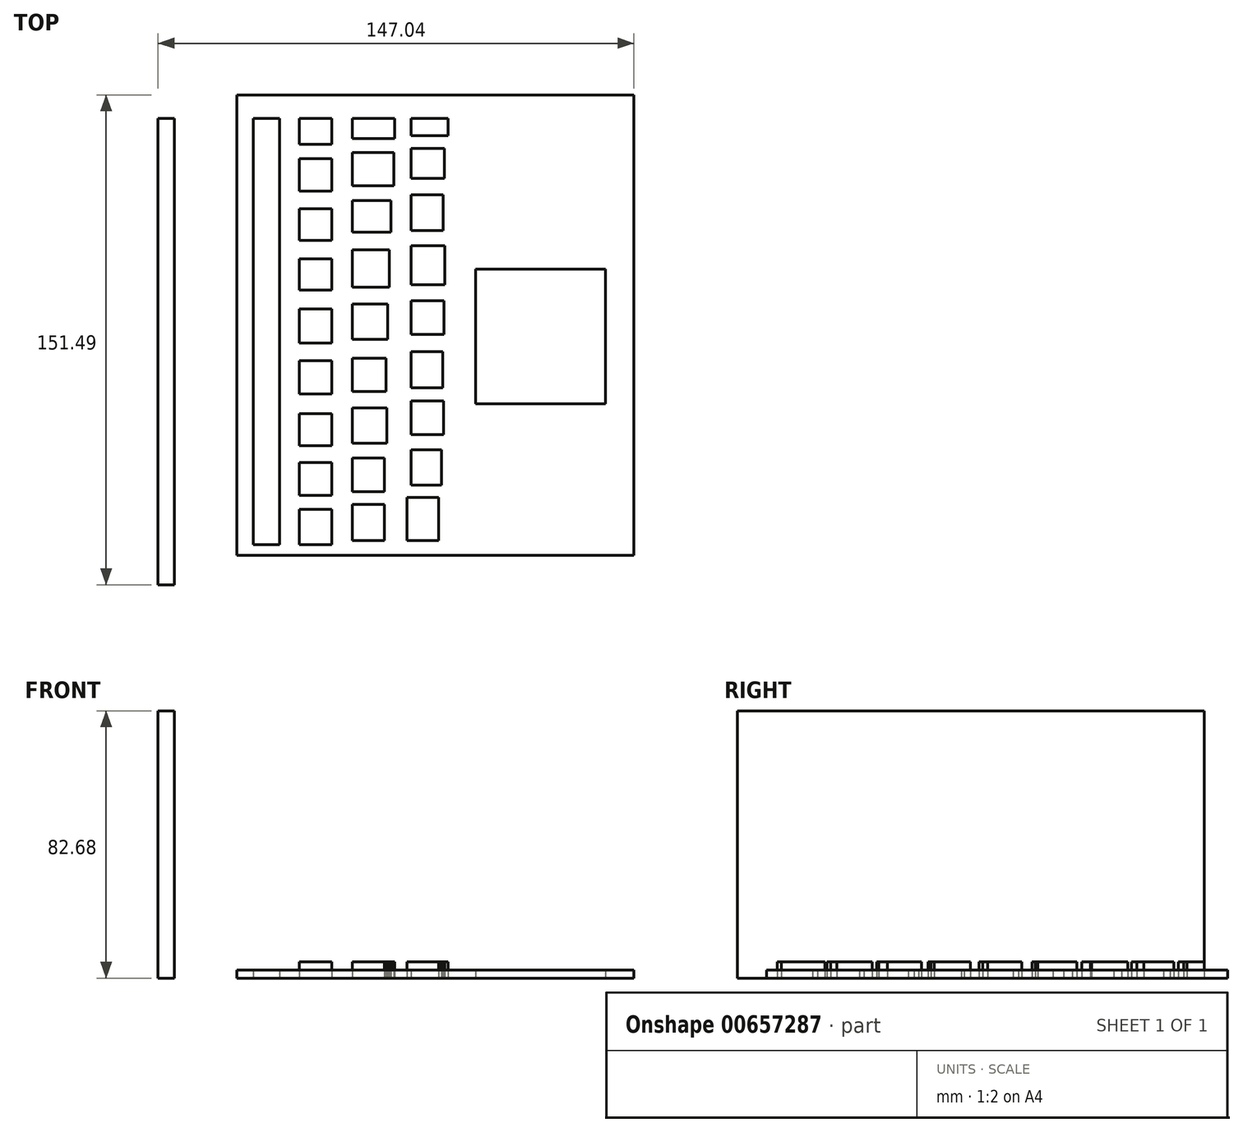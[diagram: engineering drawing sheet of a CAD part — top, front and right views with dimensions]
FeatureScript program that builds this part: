
annotation { "Feature Type Name" : "Feature", "Feature Type Description" : "" }
export const myFeature = defineFeature(function(context is Context, id is Id, definition is map)
    precondition{}
    {
        {
            var Q0;
            Q0=qCreatedBy(makeId("Right.planeOp"),FACE);
            var sketch = newSketch(context, id + "F0", { "sketchPlane" : qUnion([Q0])});
            skLineSegment(sketch, "E0.bottom", {"start": v(-144.27, 82.68) * mm, "end": v(0, 82.68) * mm});
            skLineSegment(sketch, "E0.top", {"start": v(-144.27, 0) * mm, "end": v(0, 0) * mm});
            skLineSegment(sketch, "E0.left", {"start": v(-144.27, 82.68) * mm, "end": v(-144.27, 0) * mm});
            skLineSegment(sketch, "E0.right", {"start": v(0, 82.68) * mm, "end": v(0, 0) * mm});
            skSolve(sketch);
        }
        {
            var Q0;
            Q0=qCreatedBy(makeId("Top.planeOp"),FACE);
            var sketch = newSketch(context, id + "F1", { "sketchPlane" : qUnion([Q0])});
            skLineSegment(sketch, "E1.bottom", {"start": v(24.3, -135.23) * mm, "end": v(147.04, -135.23) * mm});
            skLineSegment(sketch, "E1.top", {"start": v(24.3, 7.22) * mm, "end": v(147.04, 7.22) * mm});
            skLineSegment(sketch, "E1.left", {"start": v(24.3, -135.23) * mm, "end": v(24.3, 7.22) * mm});
            skLineSegment(sketch, "E1.right", {"start": v(147.04, -135.23) * mm, "end": v(147.04, 7.22) * mm});
            skLineSegment(sketch, "E2.bottom", {"start": v(98.13, -88.3) * mm, "end": v(138.28, -88.3) * mm});
            skLineSegment(sketch, "E2.top", {"start": v(98.13, -46.73) * mm, "end": v(138.28, -46.73) * mm});
            skLineSegment(sketch, "E2.left", {"start": v(98.13, -88.3) * mm, "end": v(98.13, -46.73) * mm});
            skLineSegment(sketch, "E2.right", {"start": v(138.28, -88.3) * mm, "end": v(138.28, -46.73) * mm});
            skLineSegment(sketch, "E3.bottom", {"start": v(29.4, -131.89) * mm, "end": v(37.55, -131.89) * mm});
            skLineSegment(sketch, "E3.top", {"start": v(29.4, 0) * mm, "end": v(37.55, 0) * mm});
            skLineSegment(sketch, "E3.left", {"start": v(29.4, -131.89) * mm, "end": v(29.4, 0) * mm});
            skLineSegment(sketch, "E3.right", {"start": v(37.55, -131.89) * mm, "end": v(37.55, 0) * mm});
            skLineSegment(sketch, "E4.bottom", {"start": v(43.69, -131.89) * mm, "end": v(53.65, -131.89) * mm});
            skLineSegment(sketch, "E4.top", {"start": v(43.69, -121.02) * mm, "end": v(53.65, -121.02) * mm});
            skLineSegment(sketch, "E4.left", {"start": v(43.69, -131.89) * mm, "end": v(43.69, -121.02) * mm});
            skLineSegment(sketch, "E4.right", {"start": v(53.65, -131.89) * mm, "end": v(53.65, -121.02) * mm});
            skLineSegment(sketch, "E5.bottom", {"start": v(43.69, -116.6) * mm, "end": v(53.65, -116.6) * mm});
            skLineSegment(sketch, "E5.top", {"start": v(43.69, -106.49) * mm, "end": v(53.65, -106.49) * mm});
            skLineSegment(sketch, "E5.left", {"start": v(43.69, -116.6) * mm, "end": v(43.69, -106.49) * mm});
            skLineSegment(sketch, "E5.right", {"start": v(53.65, -116.6) * mm, "end": v(53.65, -106.49) * mm});
            skLineSegment(sketch, "E6.bottom", {"start": v(43.69, -101.23) * mm, "end": v(53.65, -101.23) * mm});
            skLineSegment(sketch, "E6.top", {"start": v(43.69, -91.38) * mm, "end": v(53.65, -91.38) * mm});
            skLineSegment(sketch, "E6.left", {"start": v(43.69, -101.23) * mm, "end": v(43.69, -91.38) * mm});
            skLineSegment(sketch, "E6.right", {"start": v(53.65, -101.23) * mm, "end": v(53.65, -91.38) * mm});
            skLineSegment(sketch, "E7.bottom", {"start": v(43.69, -85.34) * mm, "end": v(53.65, -85.34) * mm});
            skLineSegment(sketch, "E7.top", {"start": v(43.69, -75.04) * mm, "end": v(53.65, -75.04) * mm});
            skLineSegment(sketch, "E7.left", {"start": v(43.69, -85.34) * mm, "end": v(43.69, -75.04) * mm});
            skLineSegment(sketch, "E7.right", {"start": v(53.65, -85.34) * mm, "end": v(53.65, -75.04) * mm});
            skLineSegment(sketch, "E8.bottom", {"start": v(43.69, -69.58) * mm, "end": v(53.65, -69.58) * mm});
            skLineSegment(sketch, "E8.top", {"start": v(43.69, -59) * mm, "end": v(53.65, -59) * mm});
            skLineSegment(sketch, "E8.left", {"start": v(43.69, -69.58) * mm, "end": v(43.69, -59) * mm});
            skLineSegment(sketch, "E8.right", {"start": v(53.65, -69.58) * mm, "end": v(53.65, -59) * mm});
            skLineSegment(sketch, "E9.bottom", {"start": v(43.69, -53.2) * mm, "end": v(53.65, -53.2) * mm});
            skLineSegment(sketch, "E9.top", {"start": v(43.69, -43.48) * mm, "end": v(53.65, -43.48) * mm});
            skLineSegment(sketch, "E9.left", {"start": v(43.69, -53.2) * mm, "end": v(43.69, -43.48) * mm});
            skLineSegment(sketch, "E9.right", {"start": v(53.65, -53.2) * mm, "end": v(53.65, -43.48) * mm});
            skLineSegment(sketch, "E10.bottom", {"start": v(43.69, -37.82) * mm, "end": v(53.65, -37.82) * mm});
            skLineSegment(sketch, "E10.top", {"start": v(43.69, -27.98) * mm, "end": v(53.65, -27.98) * mm});
            skLineSegment(sketch, "E10.left", {"start": v(43.69, -37.82) * mm, "end": v(43.69, -27.98) * mm});
            skLineSegment(sketch, "E10.right", {"start": v(53.65, -37.82) * mm, "end": v(53.65, -27.98) * mm});
            skLineSegment(sketch, "E11.bottom", {"start": v(43.69, -22.52) * mm, "end": v(53.65, -22.52) * mm});
            skLineSegment(sketch, "E11.top", {"start": v(43.69, -12.52) * mm, "end": v(53.65, -12.52) * mm});
            skLineSegment(sketch, "E11.left", {"start": v(43.69, -22.52) * mm, "end": v(43.69, -12.52) * mm});
            skLineSegment(sketch, "E11.right", {"start": v(53.65, -22.52) * mm, "end": v(53.65, -12.52) * mm});
            skLineSegment(sketch, "E12.bottom", {"start": v(43.69, -8.03) * mm, "end": v(53.65, -8.03) * mm});
            skLineSegment(sketch, "E12.top", {"start": v(43.69, 0) * mm, "end": v(53.65, 0) * mm});
            skLineSegment(sketch, "E12.left", {"start": v(43.69, -8.03) * mm, "end": v(43.69, 0) * mm});
            skLineSegment(sketch, "E12.right", {"start": v(53.65, -8.03) * mm, "end": v(53.65, 0) * mm});
            skLineSegment(sketch, "E13.bottom", {"start": v(60, -130.66) * mm, "end": v(69.95, -130.66) * mm});
            skLineSegment(sketch, "E13.top", {"start": v(60, -119.44) * mm, "end": v(69.95, -119.44) * mm});
            skLineSegment(sketch, "E13.left", {"start": v(60, -130.66) * mm, "end": v(60, -119.44) * mm});
            skLineSegment(sketch, "E13.right", {"start": v(69.95, -130.66) * mm, "end": v(69.95, -119.44) * mm});
            skPoint(sketch, "E14.firstSnap0", {"position": v(60, -125.05) * mm});
            skPoint(sketch, "E14.oppositeSnap0", {"position": v(69.95, -125.05) * mm});
            skLineSegment(sketch, "E14.bottom", {"start": v(60, -115.5) * mm, "end": v(69.95, -115.5) * mm});
            skLineSegment(sketch, "E14.top", {"start": v(60, -105.1) * mm, "end": v(69.95, -105.1) * mm});
            skLineSegment(sketch, "E14.left", {"start": v(60, -115.5) * mm, "end": v(60, -105.1) * mm});
            skLineSegment(sketch, "E14.right", {"start": v(69.95, -115.5) * mm, "end": v(69.95, -105.1) * mm});
            skLineSegment(sketch, "E15.bottom", {"start": v(60, -100.52) * mm, "end": v(70.74, -100.52) * mm});
            skLineSegment(sketch, "E15.top", {"start": v(60, -89.64) * mm, "end": v(70.74, -89.64) * mm});
            skLineSegment(sketch, "E15.left", {"start": v(60, -100.52) * mm, "end": v(60, -89.64) * mm});
            skLineSegment(sketch, "E15.right", {"start": v(70.74, -100.52) * mm, "end": v(70.74, -89.64) * mm});
            skLineSegment(sketch, "E16.bottom", {"start": v(60, -84.48) * mm, "end": v(70.42, -84.48) * mm});
            skLineSegment(sketch, "E16.top", {"start": v(60, -74.18) * mm, "end": v(70.42, -74.18) * mm});
            skLineSegment(sketch, "E16.left", {"start": v(60, -84.48) * mm, "end": v(60, -74.18) * mm});
            skLineSegment(sketch, "E16.right", {"start": v(70.42, -84.48) * mm, "end": v(70.42, -74.18) * mm});
            skLineSegment(sketch, "E17.bottom", {"start": v(60, -68.38) * mm, "end": v(70.93, -68.38) * mm});
            skLineSegment(sketch, "E17.top", {"start": v(60, -57.45) * mm, "end": v(70.93, -57.45) * mm});
            skLineSegment(sketch, "E17.left", {"start": v(60, -68.38) * mm, "end": v(60, -57.45) * mm});
            skLineSegment(sketch, "E17.right", {"start": v(70.93, -68.38) * mm, "end": v(70.93, -57.45) * mm});
            skLineSegment(sketch, "E18.bottom", {"start": v(60, -52.24) * mm, "end": v(71.44, -52.24) * mm});
            skLineSegment(sketch, "E18.top", {"start": v(60, -40.73) * mm, "end": v(71.44, -40.73) * mm});
            skLineSegment(sketch, "E18.left", {"start": v(60, -52.24) * mm, "end": v(60, -40.73) * mm});
            skLineSegment(sketch, "E18.right", {"start": v(71.44, -52.24) * mm, "end": v(71.44, -40.73) * mm});
            skLineSegment(sketch, "E19.bottom", {"start": v(60, -35.22) * mm, "end": v(72.05, -35.22) * mm});
            skLineSegment(sketch, "E19.top", {"start": v(60, -25.51) * mm, "end": v(72.05, -25.51) * mm});
            skLineSegment(sketch, "E19.left", {"start": v(60, -35.22) * mm, "end": v(60, -25.51) * mm});
            skLineSegment(sketch, "E19.right", {"start": v(72.05, -35.22) * mm, "end": v(72.05, -25.51) * mm});
            skLineSegment(sketch, "E20.bottom", {"start": v(60, -20.84) * mm, "end": v(72.82, -20.84) * mm});
            skLineSegment(sketch, "E20.top", {"start": v(60, -10.6) * mm, "end": v(72.82, -10.6) * mm});
            skLineSegment(sketch, "E20.left", {"start": v(60, -20.84) * mm, "end": v(60, -10.6) * mm});
            skLineSegment(sketch, "E20.right", {"start": v(72.82, -20.84) * mm, "end": v(72.82, -10.6) * mm});
            skLineSegment(sketch, "E21.bottom", {"start": v(60, -6.3) * mm, "end": v(73.1, -6.3) * mm});
            skLineSegment(sketch, "E21.top", {"start": v(60, 0) * mm, "end": v(73.1, 0) * mm});
            skLineSegment(sketch, "E21.left", {"start": v(60, -6.3) * mm, "end": v(60, 0) * mm});
            skLineSegment(sketch, "E21.right", {"start": v(73.1, -6.3) * mm, "end": v(73.1, 0) * mm});
            skLineSegment(sketch, "E22.bottom", {"start": v(76.97, -130.66) * mm, "end": v(86.66, -130.66) * mm});
            skLineSegment(sketch, "E22.top", {"start": v(76.97, -117.22) * mm, "end": v(86.66, -117.22) * mm});
            skLineSegment(sketch, "E22.left", {"start": v(76.97, -130.66) * mm, "end": v(76.97, -117.22) * mm});
            skLineSegment(sketch, "E22.right", {"start": v(86.66, -130.66) * mm, "end": v(86.66, -117.22) * mm});
            skLineSegment(sketch, "E23.bottom", {"start": v(78.24, -113.48) * mm, "end": v(87.6, -113.48) * mm});
            skLineSegment(sketch, "E23.top", {"start": v(78.24, -102.6) * mm, "end": v(87.6, -102.6) * mm});
            skLineSegment(sketch, "E23.left", {"start": v(78.24, -113.48) * mm, "end": v(78.24, -102.6) * mm});
            skLineSegment(sketch, "E23.right", {"start": v(87.6, -113.48) * mm, "end": v(87.6, -102.6) * mm});
            skLineSegment(sketch, "E24.bottom", {"start": v(78.24, -97.88) * mm, "end": v(88.2, -97.88) * mm});
            skLineSegment(sketch, "E24.top", {"start": v(78.24, -87.38) * mm, "end": v(88.2, -87.38) * mm});
            skLineSegment(sketch, "E24.left", {"start": v(78.24, -97.88) * mm, "end": v(78.24, -87.38) * mm});
            skLineSegment(sketch, "E24.right", {"start": v(88.2, -97.88) * mm, "end": v(88.2, -87.38) * mm});
            skLineSegment(sketch, "E25.bottom", {"start": v(78.24, -83.39) * mm, "end": v(88.06, -83.39) * mm});
            skLineSegment(sketch, "E25.top", {"start": v(78.24, -72.2) * mm, "end": v(88.06, -72.2) * mm});
            skLineSegment(sketch, "E25.left", {"start": v(78.24, -83.39) * mm, "end": v(78.24, -72.2) * mm});
            skLineSegment(sketch, "E25.right", {"start": v(88.06, -83.39) * mm, "end": v(88.06, -72.2) * mm});
            skLineSegment(sketch, "E26.bottom", {"start": v(78.24, -66.9) * mm, "end": v(88.32, -66.9) * mm});
            skLineSegment(sketch, "E26.top", {"start": v(78.24, -56.4) * mm, "end": v(88.32, -56.4) * mm});
            skLineSegment(sketch, "E26.left", {"start": v(78.24, -66.9) * mm, "end": v(78.24, -56.4) * mm});
            skLineSegment(sketch, "E26.right", {"start": v(88.32, -66.9) * mm, "end": v(88.32, -56.4) * mm});
            skLineSegment(sketch, "E27.bottom", {"start": v(78.24, -51.45) * mm, "end": v(88.67, -51.45) * mm});
            skLineSegment(sketch, "E27.top", {"start": v(78.24, -39.39) * mm, "end": v(88.67, -39.39) * mm});
            skLineSegment(sketch, "E27.left", {"start": v(78.24, -51.45) * mm, "end": v(78.24, -39.39) * mm});
            skLineSegment(sketch, "E27.right", {"start": v(88.67, -51.45) * mm, "end": v(88.67, -39.39) * mm});
            skLineSegment(sketch, "E28.bottom", {"start": v(78.24, -34.76) * mm, "end": v(88.18, -34.76) * mm});
            skLineSegment(sketch, "E28.top", {"start": v(78.24, -23.63) * mm, "end": v(88.18, -23.63) * mm});
            skLineSegment(sketch, "E28.left", {"start": v(78.24, -34.76) * mm, "end": v(78.24, -23.63) * mm});
            skLineSegment(sketch, "E28.right", {"start": v(88.18, -34.76) * mm, "end": v(88.18, -23.63) * mm});
            skLineSegment(sketch, "E29.bottom", {"start": v(78.24, -18.62) * mm, "end": v(88.53, -18.62) * mm});
            skLineSegment(sketch, "E29.top", {"start": v(78.24, -9.34) * mm, "end": v(88.53, -9.34) * mm});
            skLineSegment(sketch, "E29.left", {"start": v(78.24, -18.62) * mm, "end": v(78.24, -9.34) * mm});
            skLineSegment(sketch, "E29.right", {"start": v(88.53, -18.62) * mm, "end": v(88.53, -9.34) * mm});
            skLineSegment(sketch, "E30.bottom", {"start": v(78.24, -5.35) * mm, "end": v(89.58, -5.35) * mm});
            skLineSegment(sketch, "E30.top", {"start": v(78.24, 0) * mm, "end": v(89.58, 0) * mm});
            skLineSegment(sketch, "E30.left", {"start": v(78.24, -5.35) * mm, "end": v(78.24, 0) * mm});
            skLineSegment(sketch, "E30.right", {"start": v(89.58, -5.35) * mm, "end": v(89.58, 0) * mm});
            skSolve(sketch);
        }
        {
            var Q0;
            Q0=makeQuery(id+"F0.imprint","IMPRINT",FACE,{"disambiguationData":[TD([[makeQuery(id+"F0.imprint","IMPRINT",EDGE,{"derivedFrom":sQuery(id+"F0.wireOp",EDGE,"E0.bottom")}),-1.0]])]});
            extrude(context, id + "F2", {"entities" : qUnion([Q0]), "depth" : 5.08 * mm, "offsetDistance" : 25.4 * mm});
        }
        {
            var Q0;
            Q0=makeQuery(id+"F1.imprint","IMPRINT",FACE,{"disambiguationData":[TD([[makeQuery(id+"F1.imprint","IMPRINT",EDGE,{"derivedFrom":sQuery(id+"F1.wireOp",EDGE,"E2.bottom")}),1.0]])]});
            extrude(context, id + "F3", {"entities" : qUnion([Q0]), "depth" : 2.54 * mm, "offsetDistance" : 25.4 * mm});
        }
        {
            var Q0;
            Q0=makeQuery(id+"F1.imprint","IMPRINT",FACE,{"disambiguationData":[TD([[makeQuery(id+"F1.imprint","IMPRINT",EDGE,{"derivedFrom":sQuery(id+"F1.wireOp",EDGE,"E3.bottom")}),1.0]])]});
            extrude(context, id + "F4", {"entities" : qUnion([Q0]), "depth" : 2.54 * mm, "offsetDistance" : 25.4 * mm});
        }
        {
            var Q0;
            Q0=makeQuery(id+"F1.imprint","IMPRINT",FACE,{"disambiguationData":[TD([[makeQuery(id+"F1.imprint","IMPRINT",EDGE,{"derivedFrom":sQuery(id+"F1.wireOp",EDGE,"E11.bottom")}),1.0]])]});
            extrude(context, id + "F5", {"entities" : qUnion([Q0]), "depth" : 5.08 * mm, "offsetDistance" : 25.4 * mm});
        }
        {
            var Q0;
            Q0=makeQuery(id+"F1.imprint","IMPRINT",FACE,{"disambiguationData":[TD([[makeQuery(id+"F1.imprint","IMPRINT",EDGE,{"derivedFrom":sQuery(id+"F1.wireOp",EDGE,"E10.bottom")}),1.0]])]});
            extrude(context, id + "F6", {"entities" : qUnion([Q0]), "depth" : 5.08 * mm, "offsetDistance" : 25.4 * mm});
        }
        {
            var Q0;
            Q0=makeQuery(id+"F1.imprint","IMPRINT",FACE,{"disambiguationData":[TD([[makeQuery(id+"F1.imprint","IMPRINT",EDGE,{"derivedFrom":sQuery(id+"F1.wireOp",EDGE,"E8.bottom")}),1.0]])]});
            extrude(context, id + "F7", {"entities" : qUnion([Q0]), "depth" : 5.08 * mm, "offsetDistance" : 25.4 * mm});
        }
        {
            var Q0;
            Q0=makeQuery(id+"F1.imprint","IMPRINT",FACE,{"disambiguationData":[TD([[makeQuery(id+"F1.imprint","IMPRINT",EDGE,{"derivedFrom":sQuery(id+"F1.wireOp",EDGE,"E7.bottom")}),1.0]])]});
            extrude(context, id + "F8", {"entities" : qUnion([Q0]), "depth" : 5.08 * mm, "offsetDistance" : 25.4 * mm});
        }
        {
            var Q0;
            Q0=makeQuery(id+"F1.imprint","IMPRINT",FACE,{"disambiguationData":[TD([[makeQuery(id+"F1.imprint","IMPRINT",EDGE,{"derivedFrom":sQuery(id+"F1.wireOp",EDGE,"E9.bottom")}),1.0]])]});
            extrude(context, id + "F9", {"entities" : qUnion([Q0]), "depth" : 5.08 * mm, "offsetDistance" : 25.4 * mm});
        }
        {
            var Q0;
            Q0=makeQuery(id+"F1.imprint","IMPRINT",FACE,{"disambiguationData":[TD([[makeQuery(id+"F1.imprint","IMPRINT",EDGE,{"derivedFrom":sQuery(id+"F1.wireOp",EDGE,"E6.bottom")}),1.0]])]});
            extrude(context, id + "F10", {"entities" : qUnion([Q0]), "depth" : 5.08 * mm, "offsetDistance" : 25.4 * mm});
        }
        {
            var Q0;
            Q0=makeQuery(id+"F1.imprint","IMPRINT",FACE,{"disambiguationData":[TD([[makeQuery(id+"F1.imprint","IMPRINT",EDGE,{"derivedFrom":sQuery(id+"F1.wireOp",EDGE,"E5.bottom")}),1.0]])]});
            extrude(context, id + "F11", {"entities" : qUnion([Q0]), "depth" : 5.08 * mm, "offsetDistance" : 25.4 * mm});
        }
        {
            var Q0;
            Q0=makeQuery(id+"F1.imprint","IMPRINT",FACE,{"disambiguationData":[TD([[makeQuery(id+"F1.imprint","IMPRINT",EDGE,{"derivedFrom":sQuery(id+"F1.wireOp",EDGE,"E4.bottom")}),1.0]])]});
            extrude(context, id + "F12", {"entities" : qUnion([Q0]), "depth" : 5.08 * mm, "offsetDistance" : 25.4 * mm});
        }
        {
            var Q0;
            Q0=makeQuery(id+"F1.imprint","IMPRINT",FACE,{"disambiguationData":[TD([[makeQuery(id+"F1.imprint","IMPRINT",EDGE,{"derivedFrom":sQuery(id+"F1.wireOp",EDGE,"E12.bottom")}),1.0]])]});
            extrude(context, id + "F13", {"entities" : qUnion([Q0]), "depth" : 5.08 * mm, "offsetDistance" : 25.4 * mm});
        }
        {
            var Q0;
            Q0=makeQuery(id+"F1.imprint","IMPRINT",FACE,{"disambiguationData":[TD([[makeQuery(id+"F1.imprint","IMPRINT",EDGE,{"derivedFrom":sQuery(id+"F1.wireOp",EDGE,"E21.bottom")}),1.0]])]});
            extrude(context, id + "F14", {"entities" : qUnion([Q0]), "depth" : 5.08 * mm, "offsetDistance" : 25.4 * mm});
        }
        {
            var Q0;
            Q0=makeQuery(id+"F1.imprint","IMPRINT",FACE,{"disambiguationData":[TD([[makeQuery(id+"F1.imprint","IMPRINT",EDGE,{"derivedFrom":sQuery(id+"F1.wireOp",EDGE,"E20.bottom")}),1.0]])]});
            extrude(context, id + "F15", {"entities" : qUnion([Q0]), "depth" : 5.08 * mm, "offsetDistance" : 25.4 * mm});
        }
        {
            var Q0;
            Q0=makeQuery(id+"F1.imprint","IMPRINT",FACE,{"disambiguationData":[TD([[makeQuery(id+"F1.imprint","IMPRINT",EDGE,{"derivedFrom":sQuery(id+"F1.wireOp",EDGE,"E18.bottom")}),1.0]])]});
            var Q1;
            Q1=makeQuery(id+"F1.imprint","IMPRINT",FACE,{"disambiguationData":[TD([[makeQuery(id+"F1.imprint","IMPRINT",EDGE,{"derivedFrom":sQuery(id+"F1.wireOp",EDGE,"E19.bottom")}),1.0]])]});
            var Q2;
            Q2=makeQuery(id+"F1.imprint","IMPRINT",FACE,{"disambiguationData":[TD([[makeQuery(id+"F1.imprint","IMPRINT",EDGE,{"derivedFrom":sQuery(id+"F1.wireOp",EDGE,"E27.bottom")}),1.0]])]});
            var Q3;
            Q3=makeQuery(id+"F1.imprint","IMPRINT",FACE,{"disambiguationData":[TD([[makeQuery(id+"F1.imprint","IMPRINT",EDGE,{"derivedFrom":sQuery(id+"F1.wireOp",EDGE,"E26.bottom")}),1.0]])]});
            var Q4;
            Q4=makeQuery(id+"F1.imprint","IMPRINT",FACE,{"disambiguationData":[TD([[makeQuery(id+"F1.imprint","IMPRINT",EDGE,{"derivedFrom":sQuery(id+"F1.wireOp",EDGE,"E25.bottom")}),1.0]])]});
            var Q5;
            Q5=makeQuery(id+"F1.imprint","IMPRINT",FACE,{"disambiguationData":[TD([[makeQuery(id+"F1.imprint","IMPRINT",EDGE,{"derivedFrom":sQuery(id+"F1.wireOp",EDGE,"E17.bottom")}),1.0]])]});
            extrude(context, id + "F16", {"entities" : qUnion([Q0, Q1, Q2, Q3, Q4, Q5]), "depth" : 5.08 * mm, "offsetDistance" : 25.4 * mm});
        }
        {
            var Q0;
            Q0=makeQuery(id+"F1.imprint","IMPRINT",FACE,{"disambiguationData":[TD([[makeQuery(id+"F1.imprint","IMPRINT",EDGE,{"derivedFrom":sQuery(id+"F1.wireOp",EDGE,"E30.bottom")}),1.0]])]});
            var Q1;
            Q1=makeQuery(id+"F1.imprint","IMPRINT",FACE,{"disambiguationData":[TD([[makeQuery(id+"F1.imprint","IMPRINT",EDGE,{"derivedFrom":sQuery(id+"F1.wireOp",EDGE,"E29.bottom")}),1.0]])]});
            extrude(context, id + "F17", {"entities" : qUnion([Q0, Q1]), "depth" : 5.08 * mm, "offsetDistance" : 25.4 * mm});
        }
        {
            var Q0;
            Q0=makeQuery(id+"F1.imprint","IMPRINT",FACE,{"disambiguationData":[TD([[makeQuery(id+"F1.imprint","IMPRINT",EDGE,{"derivedFrom":sQuery(id+"F1.wireOp",EDGE,"E28.bottom")}),1.0]])]});
            extrude(context, id + "F18", {"entities" : qUnion([Q0]), "depth" : 5.08 * mm, "offsetDistance" : 25.4 * mm});
        }
        {
            var Q0;
            Q0=makeQuery(id+"F1.imprint","IMPRINT",FACE,{"disambiguationData":[TD([[makeQuery(id+"F1.imprint","IMPRINT",EDGE,{"derivedFrom":sQuery(id+"F1.wireOp",EDGE,"E16.bottom")}),1.0]])]});
            var Q1;
            Q1=makeQuery(id+"F1.imprint","IMPRINT",FACE,{"disambiguationData":[TD([[makeQuery(id+"F1.imprint","IMPRINT",EDGE,{"derivedFrom":sQuery(id+"F1.wireOp",EDGE,"E15.bottom")}),1.0]])]});
            var Q2;
            Q2=makeQuery(id+"F1.imprint","IMPRINT",FACE,{"disambiguationData":[TD([[makeQuery(id+"F1.imprint","IMPRINT",EDGE,{"derivedFrom":sQuery(id+"F1.wireOp",EDGE,"E23.bottom")}),1.0]])]});
            var Q3;
            Q3=makeQuery(id+"F1.imprint","IMPRINT",FACE,{"disambiguationData":[TD([[makeQuery(id+"F1.imprint","IMPRINT",EDGE,{"derivedFrom":sQuery(id+"F1.wireOp",EDGE,"E22.bottom")}),1.0]])]});
            extrude(context, id + "F19", {"entities" : qUnion([Q0, Q1, Q2, Q3]), "depth" : 5.08 * mm, "offsetDistance" : 25.4 * mm});
        }
        {
            var Q0;
            Q0=makeQuery(id+"F1.imprint","IMPRINT",FACE,{"disambiguationData":[TD([[makeQuery(id+"F1.imprint","IMPRINT",EDGE,{"derivedFrom":sQuery(id+"F1.wireOp",EDGE,"E24.bottom")}),1.0]])]});
            extrude(context, id + "F20", {"entities" : qUnion([Q0]), "depth" : 5.08 * mm, "offsetDistance" : 25.4 * mm});
        }
        {
            var Q0;
            Q0=makeQuery(id+"F1.imprint","IMPRINT",FACE,{"disambiguationData":[TD([[makeQuery(id+"F1.imprint","IMPRINT",EDGE,{"derivedFrom":sQuery(id+"F1.wireOp",EDGE,"E13.bottom")}),1.0]])]});
            var Q1;
            Q1=makeQuery(id+"F1.imprint","IMPRINT",FACE,{"disambiguationData":[TD([[makeQuery(id+"F1.imprint","IMPRINT",EDGE,{"derivedFrom":sQuery(id+"F1.wireOp",EDGE,"E14.bottom")}),1.0]])]});
            extrude(context, id + "F21", {"entities" : qUnion([Q0, Q1]), "depth" : 5.08 * mm, "offsetDistance" : 25.4 * mm});
        }
        {
            var Q0;
            Q0=makeQuery(id+"F1.imprint","IMPRINT",FACE,{"disambiguationData":[TD([[makeQuery(id+"F1.imprint","IMPRINT",EDGE,{"derivedFrom":sQuery(id+"F1.wireOp",EDGE,"E1.bottom")}),1.0]])]});
            extrude(context, id + "F22", {"entities" : qUnion([Q0]), "depth" : 2.54 * mm, "offsetDistance" : 25.4 * mm});
        }
    });
